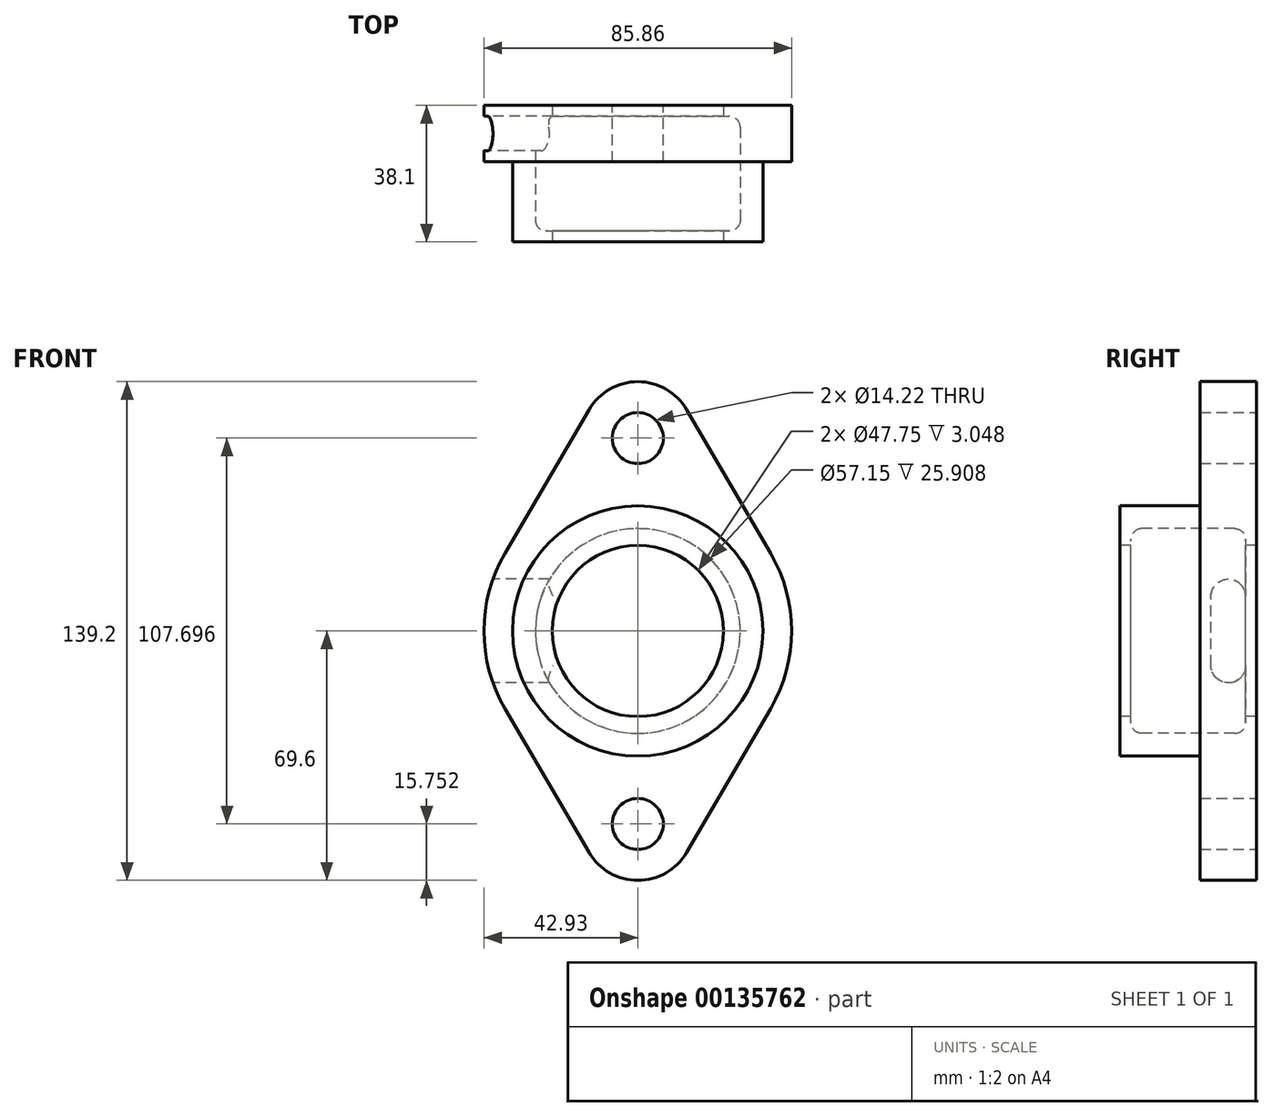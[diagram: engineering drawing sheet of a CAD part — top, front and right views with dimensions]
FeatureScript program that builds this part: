
annotation { "Feature Type Name" : "Feature", "Feature Type Description" : "" }
export const myFeature = defineFeature(function(context is Context, id is Id, definition is map)
    precondition{}
    {
        {
            var Q0;
            Q0=qCreatedBy(makeId("Front.planeOp"),FACE);
            var sketch = newSketch(context, id + "F0", { "sketchPlane" : qUnion([Q0])});
            skCircle(sketch, "E0", {"center": v(0, 0) * mm, "radius": 23.88 * mm});
            skCircle(sketch, "E1", {"center": v(0, 0) * mm, "radius": 34.93 * mm});
            skCircle(sketch, "E2", {"center": v(0, 53.85) * mm, "radius": 7.11 * mm});
            skCircle(sketch, "E3", {"center": v(0, -53.85) * mm, "radius": 7.11 * mm});
            skArc(sketch, "E4", {"start": v(-13.6, -61.8) * mm, "mid": v(0, -69.6) * mm, "end": v(13.6, -61.8) * mm});
            skArc(sketch, "E5", {"start": v(-13.6, 61.8) * mm, "mid": v(0, 69.6) * mm, "end": v(13.6, 61.8) * mm});
            skArc(sketch, "E6", {"start": v(37.06, -21.67) * mm, "mid": v(42.93, 0) * mm, "end": v(37.06, 21.67) * mm});
            skArc(sketch, "E7", {"start": v(-37.06, -21.67) * mm, "mid": v(-42.93, 0) * mm, "end": v(-37.06, 21.67) * mm});
            skLineSegment(sketch, "E8", {"start": v(-13.6, 61.8) * mm, "end": v(-37.06, 21.67) * mm});
            skLineSegment(sketch, "E9", {"start": v(13.6, 61.8) * mm, "end": v(37.06, 21.67) * mm});
            skLineSegment(sketch, "E10", {"start": v(37.06, -21.67) * mm, "end": v(13.6, -61.8) * mm});
            skLineSegment(sketch, "E11", {"start": v(-13.6, -61.8) * mm, "end": v(-37.06, -21.67) * mm});
            skSolve(sketch);
        }
        {
            var Q0;
            Q0=makeQuery(id+"F0.imprint","IMPRINT",FACE,{"disambiguationData":[TD([[makeQuery(id+"F0.imprint","IMPRINT",EDGE,{"derivedFrom":sQuery(id+"F0.wireOp",EDGE,"E1")}),-1.0]])]});
            extrude(context, id + "F1", {"entities" : qUnion([Q0]), "depth" : 15.75 * mm});
        }
        {
            var Q0;
            Q0=makeQuery(id+"F0.imprint","IMPRINT",FACE,{"disambiguationData":[TD([[makeQuery(id+"F0.imprint","IMPRINT",EDGE,{"derivedFrom":sQuery(id+"F0.wireOp",EDGE,"E0")}),-1.0]])]});
            var Q1;
            Q1=makeQuery(id+"F0.imprint","IMPRINT",FACE,{"disambiguationData":[TD([[makeQuery(id+"F0.imprint","IMPRINT",EDGE,{"derivedFrom":sQuery(id+"F0.wireOp",EDGE,"E0")}),1.0]])]});
            extrude(context, id + "F2", {"entities" : qUnion([Q0, Q1]), "operationType" : NewBodyOperationType.ADD, "depth" : 38.1 * mm});
        }
        {
            var Q0;
            Q0=qCreatedBy(makeId("Top.planeOp"),FACE);
            var sketch = newSketch(context, id + "F3", { "sketchPlane" : qUnion([Q0])});
            skLineSegment(sketch, "E12", {"start": v(28.58, -6.1) * mm, "end": v(28.58, -32) * mm});
            skLineSegment(sketch, "E13", {"start": v(0, -35.05) * mm, "end": v(0, -3.05) * mm});
            skArc(sketch, "E14", {"start": v(28.58, -32) * mm, "mid": v(27.68, -34.16) * mm, "end": v(25.53, -35.05) * mm});
            skArc(sketch, "E15", {"start": v(25.53, -3.05) * mm, "mid": v(27.68, -3.94) * mm, "end": v(28.58, -6.1) * mm});
            skLineSegment(sketch, "E16", {"start": v(25.53, -3.05) * mm, "end": v(23.88, -3.05) * mm});
            skLineSegment(sketch, "E17", {"start": v(0, -3.05) * mm, "end": v(0, 0) * mm});
            skLineSegment(sketch, "E18", {"start": v(0, 0) * mm, "end": v(23.88, 0) * mm});
            skLineSegment(sketch, "E19", {"start": v(23.88, 0) * mm, "end": v(23.88, -3.05) * mm});
            skLineSegment(sketch, "E20", {"start": v(25.53, -35.05) * mm, "end": v(23.88, -35.05) * mm});
            skLineSegment(sketch, "E21", {"start": v(23.88, -35.05) * mm, "end": v(23.88, -38.1) * mm});
            skLineSegment(sketch, "E22", {"start": v(23.88, -38.1) * mm, "end": v(0, -38.1) * mm});
            skLineSegment(sketch, "E23", {"start": v(0, -38.1) * mm, "end": v(0, -35.05) * mm});
            skLineSegment(sketch, "E24", {"start": v(0, 0) * mm, "end": v(0, -50.02) * mm, "construction": true});
            skSolve(sketch);
        }
        {
            var Q0;
            Q0=makeQuery(id+"F3.imprint","IMPRINT",FACE,{"disambiguationData":[TD([[makeQuery(id+"F3.imprint","IMPRINT",EDGE,{"derivedFrom":sQuery(id+"F3.wireOp",EDGE,"E12")}),-1.0]])]});
            var Q1;
            Q1=sQuery(id+"F3.wireOp",EDGE,"E24");
            revolve(context, id + "F4", {"operationType" : NewBodyOperationType.REMOVE, "entities" : qUnion([Q0]), "axis" : qUnion([Q1]), "revolveType" : RevolveType.FULL, "oppositeDirection" : true});
        }
        {
            var Q0;
            Q0=qCreatedBy(makeId("Right.planeOp"),FACE);
            cPlane(context, id + "F5", {"entities" : qUnion([Q0]), "cplaneType" : CPlaneType.OFFSET, "offset" : 42.93 * mm, "oppositeDirection" : true, "width" : 152.4 * mm, "height" : 152.4 * mm});
        }
        {
            var Q0;
            Q0=qCreatedBy(id+"F5.planeOp",FACE);
            var sketch = newSketch(context, id + "F6", { "sketchPlane" : qUnion([Q0])});
            skLineSegment(sketch, "E25", {"start": v(-3.05, 0) * mm, "end": v(-3.05, -9.65) * mm});
            skLineSegment(sketch, "E26", {"start": v(-12.7, 0) * mm, "end": v(-12.7, -9.65) * mm});
            skLineSegment(sketch, "E27", {"start": v(-12.7, 0) * mm, "end": v(-12.7, 9.65) * mm});
            skLineSegment(sketch, "E28", {"start": v(-3.05, 0) * mm, "end": v(-3.05, 9.65) * mm});
            skArc(sketch, "E29", {"start": v(-3.05, -9.65) * mm, "mid": v(-7.87, -14.48) * mm, "end": v(-12.7, -9.65) * mm});
            skArc(sketch, "E30", {"start": v(-3.05, 9.65) * mm, "mid": v(-7.87, 14.48) * mm, "end": v(-12.7, 9.65) * mm});
            skSolve(sketch);
        }
        {
            var Q0;
            Q0 = qSketchRegion(id + "F6", true);
            var Q1;
            Q1=qCreatedBy(makeId("Right.planeOp"),FACE);
            extrude(context, id + "F7", {"entities" : qUnion([Q0]), "operationType" : NewBodyOperationType.REMOVE, "endBound" : BoundingType.UP_TO_SURFACE, "endBoundEntityFace" : qUnion([Q1]), "depth" : 25.4 * mm});
        }
    });
